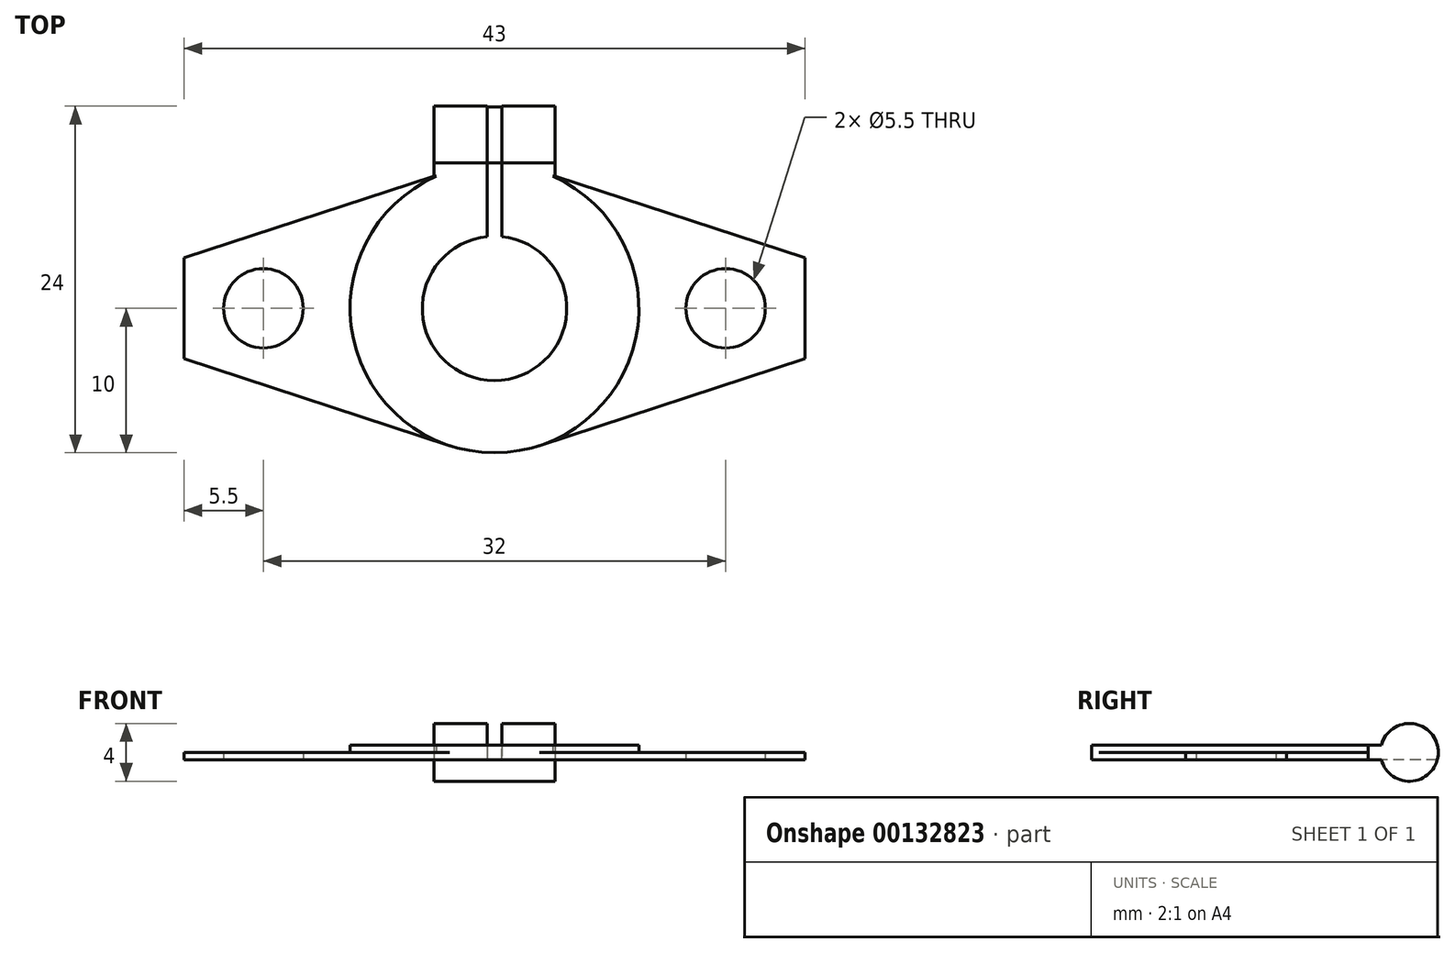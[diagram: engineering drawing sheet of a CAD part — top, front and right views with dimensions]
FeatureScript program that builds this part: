
annotation { "Feature Type Name" : "Feature", "Feature Type Description" : "" }
export const myFeature = defineFeature(function(context is Context, id is Id, definition is map)
    precondition{}
    {
        {
            assignVariable(context, id + "F0", {"name" : "t", "anyValue" : 0.5});
        }
        {
            assignVariable(context, id + "F1", {"name" : "l", "anyValue" : 1});
        }
        {
            var Q0;
            Q0=qCreatedBy(makeId("Top.planeOp"),FACE);
            var sketch = newSketch(context, id + "F2", { "sketchPlane" : qUnion([Q0])});
            skCircle(sketch, "E0", {"center": v(0, 0) * mm, "radius": 10 * mm});
            skLineSegment(sketch, "E1", {"start": v(-22.12, 14) * mm, "end": v(22.12, 14) * mm, "construction": true});
            skPoint(sketch, "E2", {"position": v(0, 14) * mm});
            skCircle(sketch, "E3", {"center": v(0, 0) * mm, "radius": 5 * mm});
            skLineSegment(sketch, "E4", {"start": v(-21.5, 0) * mm, "end": v(21.5, 0) * mm, "construction": true});
            skLineSegment(sketch, "E5", {"start": v(21.5, 3.5) * mm, "end": v(21.5, -3.5) * mm});
            skLineSegment(sketch, "E6", {"start": v(21.5, -3.5) * mm, "end": v(3.1, -9.5) * mm});
            skLineSegment(sketch, "E7", {"start": v(21.5, 3.5) * mm, "end": v(3.1, 9.5) * mm});
            skLineSegment(sketch, "E8", {"start": v(-4.2, 12) * mm, "end": v(4.2, 12) * mm});
            skPoint(sketch, "E9", {"position": v(0, 12) * mm});
            skLineSegment(sketch, "E10", {"start": v(4.2, 12) * mm, "end": v(4.2, 9.15) * mm});
            skLineSegment(sketch, "E11.MirrorCS", {"start": v(-21.5, 3.5) * mm, "end": v(-3.1, 9.5) * mm});
            skLineSegment(sketch, "E12.MirrorCS", {"start": v(-21.5, 3.5) * mm, "end": v(-21.5, -3.5) * mm});
            skLineSegment(sketch, "E13.MirrorCS", {"start": v(-21.5, -3.5) * mm, "end": v(-3.1, -9.5) * mm});
            skLineSegment(sketch, "E14.MirrorCS", {"start": v(-4.2, 12) * mm, "end": v(-4.2, 9.15) * mm});
            skCircle(sketch, "E15", {"center": v(16, 0) * mm, "radius": 2.75 * mm});
            skCircle(sketch, "E16.MirrorC", {"center": v(-16, 0) * mm, "radius": 2.75 * mm});
            skLineSegment(sketch, "E17", {"start": v(0.5, 12) * mm, "end": v(0.5, 4.97) * mm});
            skLineSegment(sketch, "E18.MirrorCS", {"start": v(-0.5, 12) * mm, "end": v(-0.5, 4.97) * mm});
            skLineSegment(sketch, "E19", {"start": v(-0.5, 12) * mm, "end": v(-0.5, 14) * mm});
            skLineSegment(sketch, "E20", {"start": v(-0.5, 14) * mm, "end": v(0.5, 14) * mm});
            skLineSegment(sketch, "E21", {"start": v(0.5, 14) * mm, "end": v(0.5, 12) * mm});
            skSolve(sketch);
        }
        {
            var Q0;
            {var subQ0=sQuery(id+"F2.wireOp",EDGE,"E12.MirrorCS");Q0=makeQuery(id+"F2.imprint","IMPRINT",FACE,{"disambiguationData":[TD([[makeQuery(id+"F2.imprint","IMPRINT",EDGE,{"derivedFrom":subQ0}),1.0]])]});}
            var Q1;
            {var subQ1=sQuery(id+"F2.wireOp",EDGE,"E5");Q1=makeQuery(id+"F2.imprint","IMPRINT",FACE,{"disambiguationData":[TD([[makeQuery(id+"F2.imprint","IMPRINT",EDGE,{"derivedFrom":subQ1}),-1.0]])]});}
            var Q2;
            {var subQ0=sQuery(id+"F2.wireOp",EDGE,"E0");var subQ6=makeQuery(id+"F2.imprint","INTERSECT",VERTEX,{"derivedFrom":[subQ0,sQuery(id+"F2.wireOp",EDGE,"E7")]});Q2=makeQuery(id+"F2.imprint","IMPRINT",FACE,{"disambiguationData":[TD([[makeQuery(id+"F2.imprint","IMPRINT",EDGE,{"disambiguationData":[TD([[subQ6,-1.0]])],"derivedFrom":subQ0}),1.0]])]});}
            var Q3;
            {var subQ0=sQuery(id+"F2.wireOp",EDGE,"E10");Q3=makeQuery(id+"F2.imprint","IMPRINT",FACE,{"disambiguationData":[TD([[makeQuery(id+"F2.imprint","IMPRINT",EDGE,{"derivedFrom":subQ0}),-1.0]])]});}
            var Q4;
            {var subQ0=sQuery(id+"F2.wireOp",EDGE,"E14.MirrorCS");Q4=makeQuery(id+"F2.imprint","IMPRINT",FACE,{"disambiguationData":[TD([[makeQuery(id+"F2.imprint","IMPRINT",EDGE,{"derivedFrom":subQ0}),1.0]])]});}
            var Q5;
            {var subQ0=sQuery(id+"F2.wireOp",EDGE,"E17");var subQ1=sQuery(id+"F2.wireOp",EDGE,"E0");var subQ2=makeQuery(id+"F2.imprint","INTERSECT",VERTEX,{"derivedFrom":[subQ1,subQ0]});Q5=makeQuery(id+"F2.imprint","IMPRINT",FACE,{"disambiguationData":[TD([[makeQuery(id+"F2.imprint","IMPRINT",EDGE,{"disambiguationData":[TD([[subQ2,-1.0]])],"derivedFrom":subQ1}),1.0]])]});}
            var Q6;
            {var subQ0=sQuery(id+"F2.wireOp",EDGE,"E17");var subQ1=sQuery(id+"F2.wireOp",EDGE,"E0");var subQ2=makeQuery(id+"F2.imprint","INTERSECT",VERTEX,{"derivedFrom":[subQ1,subQ0]});Q6=makeQuery(id+"F2.imprint","IMPRINT",FACE,{"disambiguationData":[TD([[makeQuery(id+"F2.imprint","IMPRINT",EDGE,{"disambiguationData":[TD([[subQ2,-1.0]])],"derivedFrom":subQ1}),-1.0]])]});}
            extrude(context, id + "F3", {"entities" : qUnion([Q0, Q1, Q2, Q3, Q4, Q5, Q6]), "depth" : (getVariable(context, 't')) * mm});
        }
        {
            var Q0;
            {var subQ0=sQuery(id+"F2.wireOp",EDGE,"E0");var subQ6=makeQuery(id+"F2.imprint","INTERSECT",VERTEX,{"derivedFrom":[subQ0,sQuery(id+"F2.wireOp",EDGE,"E7")]});Q0=makeQuery(id+"F2.imprint","IMPRINT",FACE,{"disambiguationData":[TD([[makeQuery(id+"F2.imprint","IMPRINT",EDGE,{"disambiguationData":[TD([[subQ6,-1.0]])],"derivedFrom":subQ0}),1.0]])]});}
            var Q1;
            {var subQ0=sQuery(id+"F2.wireOp",EDGE,"E14.MirrorCS");Q1=makeQuery(id+"F2.imprint","IMPRINT",FACE,{"disambiguationData":[TD([[makeQuery(id+"F2.imprint","IMPRINT",EDGE,{"derivedFrom":subQ0}),1.0]])]});}
            var Q2;
            {var subQ0=sQuery(id+"F2.wireOp",EDGE,"E10");Q2=makeQuery(id+"F2.imprint","IMPRINT",FACE,{"disambiguationData":[TD([[makeQuery(id+"F2.imprint","IMPRINT",EDGE,{"derivedFrom":subQ0}),-1.0]])]});}
            var Q3;
            {var subQ0=sQuery(id+"F2.wireOp",EDGE,"E17");var subQ1=sQuery(id+"F2.wireOp",EDGE,"E0");var subQ2=makeQuery(id+"F2.imprint","INTERSECT",VERTEX,{"derivedFrom":[subQ1,subQ0]});Q3=makeQuery(id+"F2.imprint","IMPRINT",FACE,{"disambiguationData":[TD([[makeQuery(id+"F2.imprint","IMPRINT",EDGE,{"disambiguationData":[TD([[subQ2,-1.0]])],"derivedFrom":subQ1}),-1.0]])]});}
            var Q4;
            {var subQ0=sQuery(id+"F2.wireOp",EDGE,"E17");var subQ1=sQuery(id+"F2.wireOp",EDGE,"E0");var subQ2=makeQuery(id+"F2.imprint","INTERSECT",VERTEX,{"derivedFrom":[subQ1,subQ0]});Q4=makeQuery(id+"F2.imprint","IMPRINT",FACE,{"disambiguationData":[TD([[makeQuery(id+"F2.imprint","IMPRINT",EDGE,{"disambiguationData":[TD([[subQ2,-1.0]])],"derivedFrom":subQ1}),1.0]])]});}
            extrude(context, id + "F4", {"entities" : qUnion([Q0, Q1, Q2, Q3, Q4]), "operationType" : NewBodyOperationType.ADD, "depth" : (getVariable(context, 'l')) * mm});
        }
        {
            var Q0;
            Q0=qCreatedBy(makeId("Top.planeOp"),FACE);
            cPlane(context, id + "F5", {"entities" : qUnion([Q0]), "cplaneType" : CPlaneType.OFFSET, "offset" : (getVariable(context, 'l') / 2) * mm, "width" : 150 * mm, "height" : 150 * mm});
        }
        {
            var Q0;
            Q0=qCreatedBy(id+"F5.planeOp",FACE);
            var sketch = newSketch(context, id + "F6", { "sketchPlane" : qUnion([Q0])});
            skLineSegment(sketch, "E22.0", {"start": v(-4.2, 12) * mm, "end": v(4.2, 12) * mm, "construction": true});
            skLineSegment(sketch, "E23.0", {"start": v(-22.12, 14) * mm, "end": v(22.12, 14) * mm, "construction": true});
            skLineSegment(sketch, "E24", {"start": v(-4.2, 12) * mm, "end": v(-4.2, 14) * mm});
            skLineSegment(sketch, "E25", {"start": v(-4.2, 14) * mm, "end": v(4.2, 14) * mm});
            skLineSegment(sketch, "E26", {"start": v(4.2, 14) * mm, "end": v(4.2, 12) * mm});
            skLineSegment(sketch, "E27", {"start": v(-4.2, 12) * mm, "end": v(4.2, 12) * mm});
            skSolve(sketch);
        }
        {
            var Q0;
            Q0=makeQuery(id+"F6.imprint","IMPRINT",FACE,{"disambiguationData":[TD([[makeQuery(id+"F6.imprint","IMPRINT",EDGE,{"derivedFrom":sQuery(id+"F6.wireOp",EDGE,"E24")}),-1.0]])]});
            var Q1;
            Q1=sQuery(id+"F6.wireOp",EDGE,"E27");
            revolve(context, id + "F7", {"operationType" : NewBodyOperationType.ADD, "entities" : qUnion([Q0]), "axis" : qUnion([Q1]), "revolveType" : RevolveType.FULL});
        }
        {
            var Q0;
            {var subQ0=sQuery(id+"F2.wireOp",EDGE,"E10");Q0=makeQuery(id+"F7.boolean.opBoolean","MERGE",FACE,{"derivedFrom":[makeQuery(id+"F4.boolean.opBoolean","MERGE",FACE,{"derivedFrom":[makeQuery(id+"F3.opExtrude","SWEPT_FACE",FACE,{"disambiguationData":[OSD([subQ0])]}),makeQuery(id+"F4.opExtrude","SWEPT_FACE",FACE,{"disambiguationData":[OSD([subQ0])]})]}),makeQuery(id+"F7.opRevolve","SWEPT_FACE",FACE,{"disambiguationData":[OSD([sQuery(id+"F6.wireOp",EDGE,"E26")])]})]});}
            var sketch = newSketch(context, id + "F8", { "sketchPlane" : qUnion([Q0])});
            skPoint(sketch, "E28.endSnap0", {"position": v(14, 5) * mm});
            skLineSegment(sketch, "E29", {"start": v(12, 0) * mm, "end": v(13.83, 4.2) * mm});
            skLineSegment(sketch, "E30", {"start": v(12, 10) * mm, "end": v(13.83, 5.8) * mm});
            skSolve(sketch);
        }
        {
            var Q0;
            Q0 = qSketchRegion(id + "F8", true);
            var Q1;
            {var subQ0=sQuery(id+"F2.wireOp",EDGE,"E10");Q1=makeQuery(id+"F8.imprint","IMPRINT",FACE,{"disambiguationData":[TD([[makeQuery(id+"F8.imprint","IMPRINT",EDGE,{"derivedFrom":makeQuery(id+"F3.opExtrude","CAP_EDGE",EDGE,{"disambiguationData":[OSD([subQ0])],"isStart":true})}),-1.0]])]});}
            var Q2;
            {var subQ0=sQuery(id+"F8.wireOp",EDGE,"E30");Q2=makeQuery(id+"F8.imprint","IMPRINT",FACE,{"disambiguationData":[TD([[makeQuery(id+"F8.imprint","IMPRINT",EDGE,{"derivedFrom":subQ0}),-1.0]])]});}
            var Q3;
            {var subQ0=sQuery(id+"F8.wireOp",EDGE,"E29");Q3=makeQuery(id+"F8.imprint","IMPRINT",FACE,{"disambiguationData":[TD([[makeQuery(id+"F8.imprint","IMPRINT",EDGE,{"derivedFrom":subQ0}),1.0]])]});}
            var Q4;
            {var subQ0=sQuery(id+"F2.wireOp",EDGE,"E14.MirrorCS");Q4=makeQuery(id+"F7.boolean.opBoolean","MERGE",FACE,{"derivedFrom":[makeQuery(id+"F4.boolean.opBoolean","MERGE",FACE,{"derivedFrom":[makeQuery(id+"F3.opExtrude","SWEPT_FACE",FACE,{"disambiguationData":[OSD([subQ0])]}),makeQuery(id+"F4.opExtrude","SWEPT_FACE",FACE,{"disambiguationData":[OSD([subQ0])]})]}),makeQuery(id+"F7.opRevolve","SWEPT_FACE",FACE,{"disambiguationData":[OSD([sQuery(id+"F6.wireOp",EDGE,"E24")])]})]});}
            extrude(context, id + "F9", {"entities" : qUnion([Q0, Q1, Q2, Q3]), "operationType" : NewBodyOperationType.ADD, "endBound" : BoundingType.UP_TO_SURFACE, "oppositeDirection" : true, "endBoundEntityFace" : qUnion([Q4]), "depth" : 25 * mm});
        }
        {
            var Q0;
            {var subQ2=sQuery(id+"F2.wireOp",EDGE,"E19");Q0=makeQuery(id+"F2.imprint","IMPRINT",FACE,{"disambiguationData":[TD([[makeQuery(id+"F2.imprint","IMPRINT",EDGE,{"derivedFrom":subQ2}),-1.0]])]});}
            var Q1;
            {var subQ0=sQuery(id+"F2.wireOp",EDGE,"E17");var subQ1=sQuery(id+"F2.wireOp",EDGE,"E0");var subQ2=makeQuery(id+"F2.imprint","INTERSECT",VERTEX,{"derivedFrom":[subQ1,subQ0]});Q1=makeQuery(id+"F2.imprint","IMPRINT",FACE,{"disambiguationData":[TD([[makeQuery(id+"F2.imprint","IMPRINT",EDGE,{"disambiguationData":[TD([[subQ2,-1.0]])],"derivedFrom":subQ1}),-1.0]])]});}
            var Q2;
            {var subQ0=sQuery(id+"F2.wireOp",EDGE,"E17");var subQ1=sQuery(id+"F2.wireOp",EDGE,"E0");var subQ2=makeQuery(id+"F2.imprint","INTERSECT",VERTEX,{"derivedFrom":[subQ1,subQ0]});Q2=makeQuery(id+"F2.imprint","IMPRINT",FACE,{"disambiguationData":[TD([[makeQuery(id+"F2.imprint","IMPRINT",EDGE,{"disambiguationData":[TD([[subQ2,-1.0]])],"derivedFrom":subQ1}),1.0]])]});}
            extrude(context, id + "F10", {"entities" : qUnion([Q0, Q1, Q2]), "operationType" : NewBodyOperationType.REMOVE, "endBound" : BoundingType.THROUGH_ALL, "depth" : 25 * mm});
        }
    });
